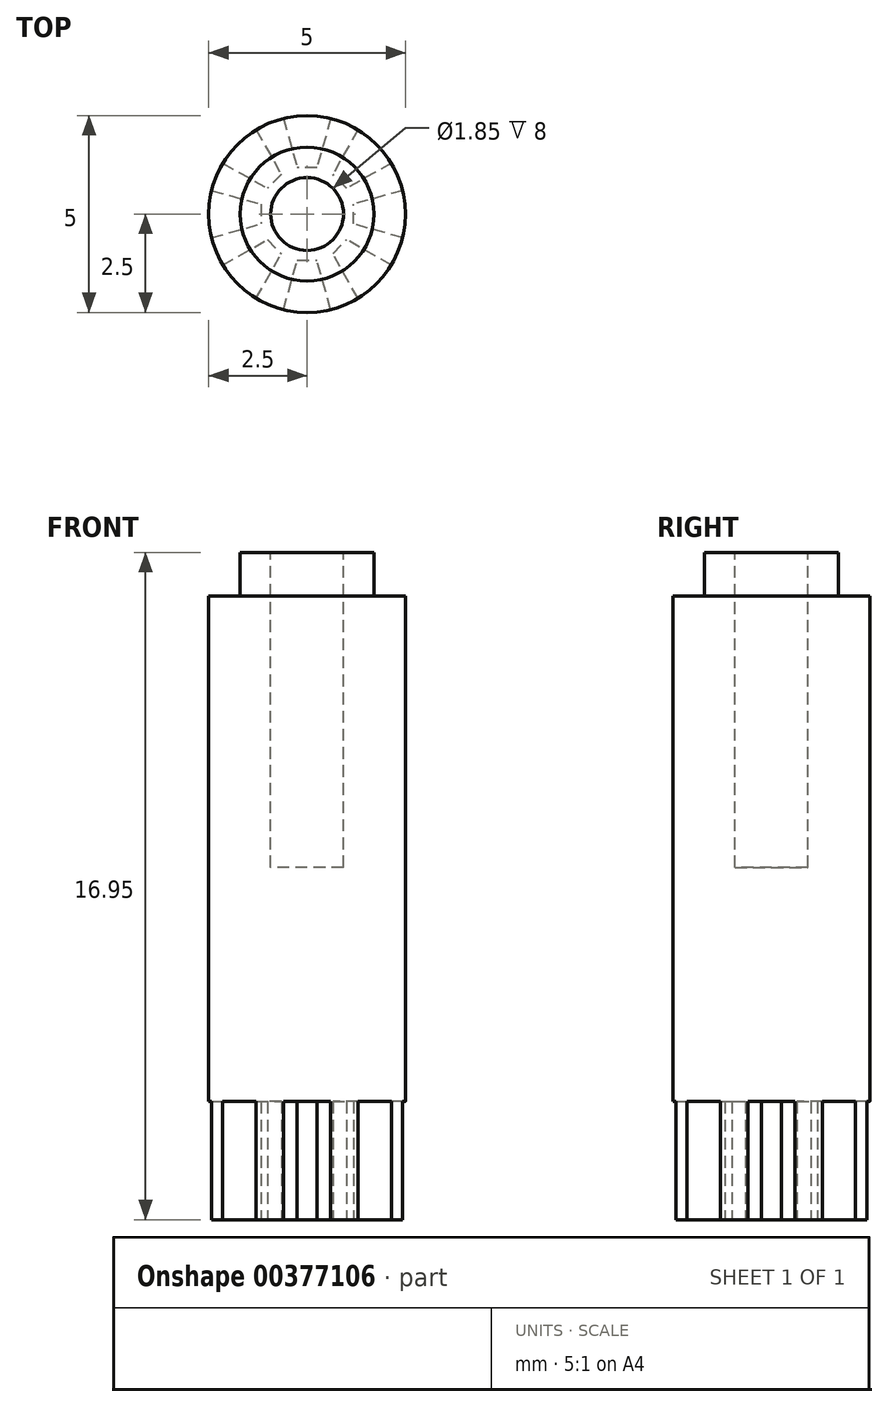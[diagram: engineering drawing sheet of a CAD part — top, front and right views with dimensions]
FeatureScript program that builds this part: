
annotation { "Feature Type Name" : "Feature", "Feature Type Description" : "" }
export const myFeature = defineFeature(function(context is Context, id is Id, definition is map)
    precondition{}
    {
        {
            var Q0;
            Q0=qCreatedBy(makeId("Top.planeOp"),FACE);
            var sketch = newSketch(context, id + "F0", { "sketchPlane" : qUnion([Q0])});
            skCircle(sketch, "E0", {"center": v(0, 0) * mm, "radius": 2.5 * mm});
            skSolve(sketch);
        }
        {
            var Q0;
            Q0 = qSketchRegion(id + "F0", true);
            extrude(context, id + "F1", {"entities" : qUnion([Q0]), "oppositeDirection" : true, "depth" : 16.95 * mm});
        }
        {
            var Q0;
            Q0=makeQuery(id+"F1.opExtrude","CAP_FACE",FACE,{"disambiguationData":[OSD([sQuery(id+"F0.wireOp",EDGE,"E0")])],"isStart":true});
            var sketch = newSketch(context, id + "F2", { "sketchPlane" : qUnion([Q0])});
            skCircle(sketch, "E1", {"center": v(0, 0) * mm, "radius": 1.7 * mm});
            skCircle(sketch, "E2.0", {"center": v(0, 0) * mm, "radius": 2.5 * mm});
            skSolve(sketch);
        }
        {
            var Q0;
            Q0 = qSketchRegion(id + "F2", true);
            extrude(context, id + "F3", {"entities" : qUnion([Q0]), "operationType" : NewBodyOperationType.REMOVE, "oppositeDirection" : true, "depth" : 1.1 * mm});
        }
        {
            var Q0;
            Q0=makeQuery(id+"F1.opExtrude","CAP_FACE",FACE,{"disambiguationData":[OSD([sQuery(id+"F0.wireOp",EDGE,"E0")])],"isStart":false});
            var sketch = newSketch(context, id + "F4", { "sketchPlane" : qUnion([Q0])});
            skLineSegment(sketch, "E3", {"start": v(0, 2.5) * mm, "end": v(0, 1.17) * mm, "construction": true});
            skLineSegment(sketch, "E4", {"start": v(-0.6, 2.43) * mm, "end": v(-0.25, 1.17) * mm});
            skLineSegment(sketch, "E5", {"start": v(-0.25, 1.17) * mm, "end": v(0, 1.17) * mm});
            skLineSegment(sketch, "E6.MirrorCS", {"start": v(0.6, 2.43) * mm, "end": v(0.25, 1.17) * mm});
            skLineSegment(sketch, "E7.MirrorCS", {"start": v(0.25, 1.17) * mm, "end": v(0, 1.17) * mm});
            skArc(sketch, "E8.0", {"start": v(0.6, 2.43) * mm, "mid": v(0, 2.5) * mm, "end": v(-0.6, 2.43) * mm});
            skSolve(sketch);
        }
        {
            var Q0;
            Q0 = qSketchRegion(id + "F4", true);
            extrude(context, id + "F5", {"entities" : qUnion([Q0]), "oppositeDirection" : true, "depth" : 3 * mm});
        }
        {
            var Q0;
            Q0=makeQuery(id+"F5.opExtrude","SWEPT_BODY",BODY,{"disambiguationData":[OSD([sQuery(id+"F4.wireOp",EDGE,"E4"),sQuery(id+"F4.wireOp",EDGE,"E5"),sQuery(id+"F4.wireOp",EDGE,"E6.MirrorCS"),sQuery(id+"F4.wireOp",EDGE,"E7.MirrorCS"),sQuery(id+"F4.wireOp",EDGE,"E8.0")])]});
            var Q1;
            Q1=makeQuery(id+"F1.opExtrude","CAP_EDGE",EDGE,{"disambiguationData":[OSD([sQuery(id+"F0.wireOp",EDGE,"E0")])],"isStart":false});
            circularPattern(context, id + "F6", {"operationType" : NewBodyOperationType.REMOVE, "entities" : qUnion([Q0]), "axis" : qUnion([Q1]), "angle" : 360 * degree, "instanceCount" : 8, "equalSpace" : true});
        }
        {
            var Q0;
            Q0=makeQuery(id+"F1.opExtrude","CAP_FACE",FACE,{"disambiguationData":[OSD([sQuery(id+"F0.wireOp",EDGE,"E0")])],"isStart":true});
            var sketch = newSketch(context, id + "F7", { "sketchPlane" : qUnion([Q0])});
            skCircle(sketch, "E9", {"center": v(0, 0) * mm, "radius": 0.93 * mm});
            skSolve(sketch);
        }
        {
            var Q0;
            Q0 = qSketchRegion(id + "F7", true);
            extrude(context, id + "F8", {"entities" : qUnion([Q0]), "operationType" : NewBodyOperationType.REMOVE, "oppositeDirection" : true, "depth" : 8 * mm});
        }
    });
